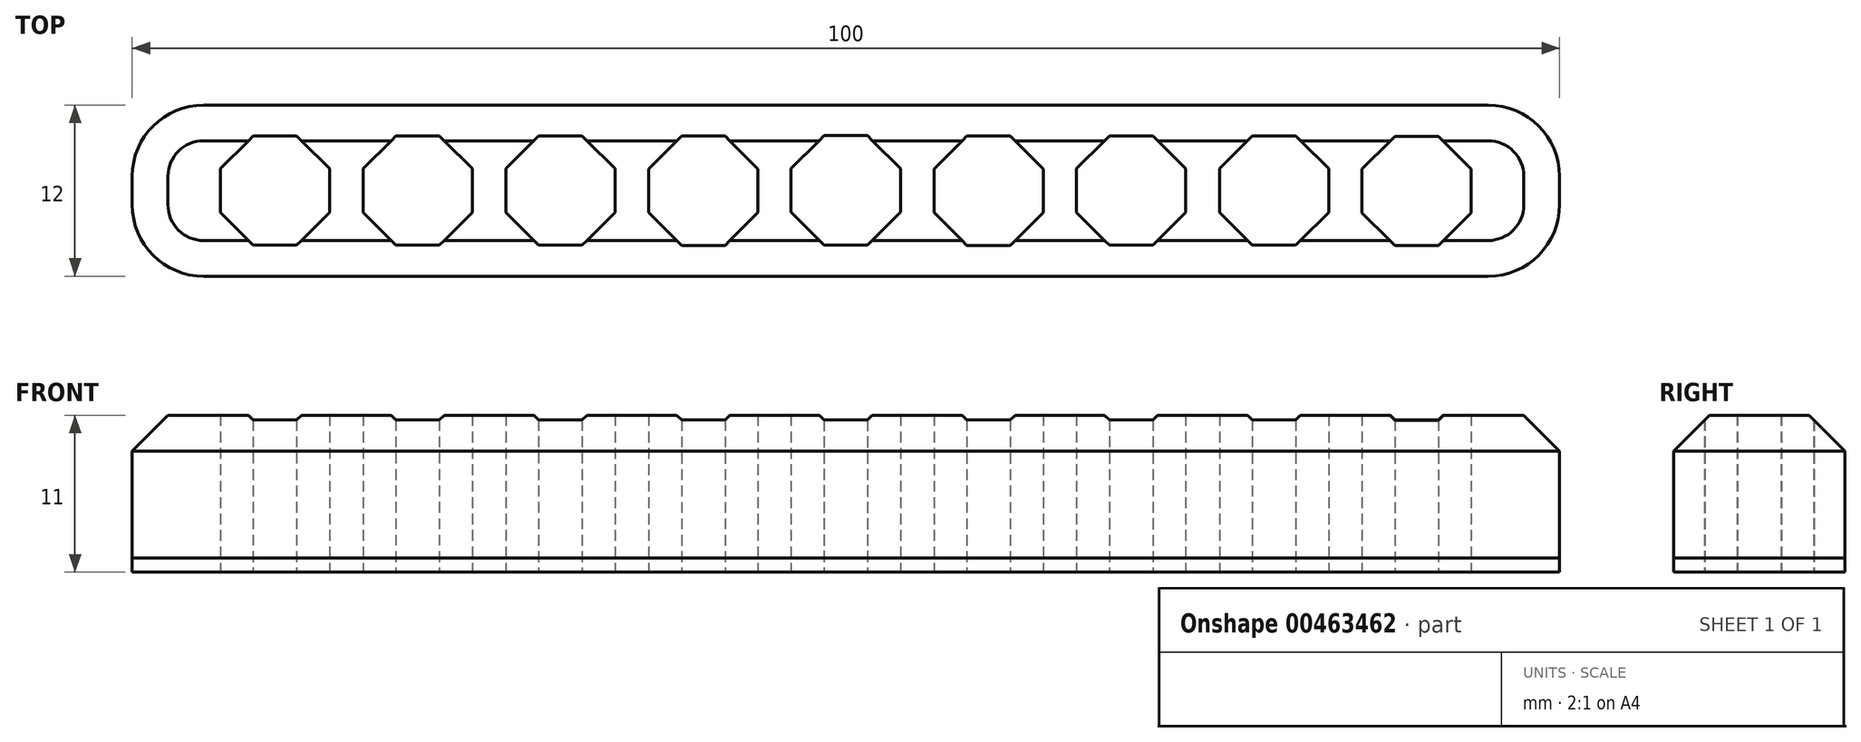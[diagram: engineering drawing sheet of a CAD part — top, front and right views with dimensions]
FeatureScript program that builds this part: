
annotation { "Feature Type Name" : "Feature", "Feature Type Description" : "" }
export const myFeature = defineFeature(function(context is Context, id is Id, definition is map)
    precondition{}
    {
        {
            var Q0;
            Q0=qCreatedBy(makeId("Top.planeOp"),FACE);
            var sketch = newSketch(context, id + "F0", { "sketchPlane" : qUnion([Q0])});
            skLineSegment(sketch, "E0.bottom", {"start": v(50, -6) * mm, "end": v(-50, -6) * mm});
            skLineSegment(sketch, "E0.top", {"start": v(50, 6) * mm, "end": v(-50, 6) * mm});
            skLineSegment(sketch, "E0.left", {"start": v(50, -6) * mm, "end": v(50, 6) * mm});
            skLineSegment(sketch, "E0.right", {"start": v(-50, -6) * mm, "end": v(-50, 6) * mm});
            skPoint(sketch, "E0.middle", {"position": v(0, 0) * mm});
            skPoint(sketch, "E1.middle", {"position": v(-40, 0) * mm});
            skLineSegment(sketch, "E2.bottom", {"start": v(-41.53, 3.83) * mm, "end": v(-38.47, 3.83) * mm});
            skLineSegment(sketch, "E2.top", {"start": v(-41.53, -3.83) * mm, "end": v(-38.47, -3.83) * mm});
            skLineSegment(sketch, "E2.left", {"start": v(-41.53, 3.83) * mm, "end": v(-41.53, -3.83) * mm});
            skLineSegment(sketch, "E2.right", {"start": v(-38.47, 3.83) * mm, "end": v(-38.47, -3.83) * mm});
            skLineSegment(sketch, "E3.bottom", {"start": v(-36.17, -1.54) * mm, "end": v(-43.83, -1.54) * mm});
            skLineSegment(sketch, "E3.top", {"start": v(-36.17, 1.54) * mm, "end": v(-43.83, 1.54) * mm});
            skLineSegment(sketch, "E3.left", {"start": v(-36.17, -1.54) * mm, "end": v(-36.17, 1.54) * mm});
            skLineSegment(sketch, "E3.right", {"start": v(-43.83, -1.54) * mm, "end": v(-43.83, 1.54) * mm});
            skPoint(sketch, "E4.middle", {"position": v(-30, 0) * mm});
            skLineSegment(sketch, "E5.bottom", {"start": v(-31.53, 3.83) * mm, "end": v(-28.47, 3.83) * mm});
            skLineSegment(sketch, "E5.top", {"start": v(-31.53, -3.83) * mm, "end": v(-28.47, -3.83) * mm});
            skLineSegment(sketch, "E5.left", {"start": v(-31.53, 3.83) * mm, "end": v(-31.53, -3.83) * mm});
            skLineSegment(sketch, "E5.right", {"start": v(-28.47, 3.83) * mm, "end": v(-28.47, -3.83) * mm});
            skLineSegment(sketch, "E6.bottom", {"start": v(-26.17, -1.54) * mm, "end": v(-33.83, -1.54) * mm});
            skLineSegment(sketch, "E6.top", {"start": v(-26.17, 1.54) * mm, "end": v(-33.83, 1.54) * mm});
            skLineSegment(sketch, "E6.left", {"start": v(-26.17, -1.54) * mm, "end": v(-26.17, 1.54) * mm});
            skLineSegment(sketch, "E6.right", {"start": v(-33.83, -1.54) * mm, "end": v(-33.83, 1.54) * mm});
            skPoint(sketch, "E7.middle", {"position": v(-20, 0) * mm});
            skLineSegment(sketch, "E8.bottom", {"start": v(-21.53, 3.84) * mm, "end": v(-18.48, 3.84) * mm});
            skLineSegment(sketch, "E8.top", {"start": v(-21.53, -3.83) * mm, "end": v(-18.48, -3.83) * mm});
            skLineSegment(sketch, "E8.left", {"start": v(-21.53, 3.84) * mm, "end": v(-21.53, -3.83) * mm});
            skLineSegment(sketch, "E8.right", {"start": v(-18.48, 3.84) * mm, "end": v(-18.48, -3.83) * mm});
            skLineSegment(sketch, "E9.bottom", {"start": v(-16.18, -1.53) * mm, "end": v(-23.83, -1.53) * mm});
            skLineSegment(sketch, "E9.top", {"start": v(-16.18, 1.54) * mm, "end": v(-23.83, 1.54) * mm});
            skLineSegment(sketch, "E9.left", {"start": v(-16.18, -1.53) * mm, "end": v(-16.18, 1.54) * mm});
            skLineSegment(sketch, "E9.right", {"start": v(-23.83, -1.53) * mm, "end": v(-23.83, 1.54) * mm});
            skPoint(sketch, "E10.middle", {"position": v(-9.99, 0) * mm});
            skLineSegment(sketch, "E11.bottom", {"start": v(-11.52, 3.83) * mm, "end": v(-8.46, 3.83) * mm});
            skLineSegment(sketch, "E11.top", {"start": v(-11.52, -3.84) * mm, "end": v(-8.46, -3.84) * mm});
            skLineSegment(sketch, "E11.left", {"start": v(-11.52, 3.83) * mm, "end": v(-11.52, -3.84) * mm});
            skLineSegment(sketch, "E11.right", {"start": v(-8.46, 3.83) * mm, "end": v(-8.46, -3.84) * mm});
            skLineSegment(sketch, "E12.bottom", {"start": v(-6.16, -1.54) * mm, "end": v(-13.82, -1.54) * mm});
            skLineSegment(sketch, "E12.top", {"start": v(-6.16, 1.53) * mm, "end": v(-13.82, 1.53) * mm});
            skLineSegment(sketch, "E12.left", {"start": v(-6.16, -1.54) * mm, "end": v(-6.16, 1.53) * mm});
            skLineSegment(sketch, "E12.right", {"start": v(-13.82, -1.54) * mm, "end": v(-13.82, 1.53) * mm});
            skPoint(sketch, "E13.middle", {"position": v(0, 0.02) * mm});
            skLineSegment(sketch, "E14.bottom", {"start": v(-1.53, 3.86) * mm, "end": v(1.52, 3.86) * mm});
            skLineSegment(sketch, "E14.top", {"start": v(-1.53, -3.8) * mm, "end": v(1.52, -3.8) * mm});
            skLineSegment(sketch, "E14.left", {"start": v(-1.53, 3.86) * mm, "end": v(-1.53, -3.8) * mm});
            skLineSegment(sketch, "E14.right", {"start": v(1.52, 3.86) * mm, "end": v(1.52, -3.8) * mm});
            skLineSegment(sketch, "E15.bottom", {"start": v(3.82, -1.51) * mm, "end": v(-3.83, -1.51) * mm});
            skLineSegment(sketch, "E15.top", {"start": v(3.82, 1.56) * mm, "end": v(-3.83, 1.56) * mm});
            skLineSegment(sketch, "E15.left", {"start": v(3.82, -1.51) * mm, "end": v(3.82, 1.56) * mm});
            skLineSegment(sketch, "E15.right", {"start": v(-3.83, -1.51) * mm, "end": v(-3.83, 1.56) * mm});
            skPoint(sketch, "E16.middle", {"position": v(10, 0) * mm});
            skLineSegment(sketch, "E17.bottom", {"start": v(8.48, 3.83) * mm, "end": v(11.53, 3.83) * mm});
            skLineSegment(sketch, "E17.top", {"start": v(8.48, -3.84) * mm, "end": v(11.53, -3.84) * mm});
            skLineSegment(sketch, "E17.left", {"start": v(8.48, 3.83) * mm, "end": v(8.48, -3.84) * mm});
            skLineSegment(sketch, "E17.right", {"start": v(11.53, 3.83) * mm, "end": v(11.53, -3.84) * mm});
            skLineSegment(sketch, "E18.bottom", {"start": v(13.83, -1.54) * mm, "end": v(6.18, -1.54) * mm});
            skLineSegment(sketch, "E18.top", {"start": v(13.83, 1.53) * mm, "end": v(6.18, 1.53) * mm});
            skLineSegment(sketch, "E18.left", {"start": v(13.83, -1.54) * mm, "end": v(13.83, 1.53) * mm});
            skLineSegment(sketch, "E18.right", {"start": v(6.18, -1.54) * mm, "end": v(6.18, 1.53) * mm});
            skPoint(sketch, "E19.middle", {"position": v(19.99, 0) * mm});
            skLineSegment(sketch, "E20.bottom", {"start": v(18.46, 3.84) * mm, "end": v(21.51, 3.84) * mm});
            skLineSegment(sketch, "E20.top", {"start": v(18.46, -3.82) * mm, "end": v(21.51, -3.82) * mm});
            skLineSegment(sketch, "E20.left", {"start": v(18.46, 3.84) * mm, "end": v(18.46, -3.82) * mm});
            skLineSegment(sketch, "E20.right", {"start": v(21.51, 3.84) * mm, "end": v(21.51, -3.82) * mm});
            skLineSegment(sketch, "E21.bottom", {"start": v(23.82, -1.53) * mm, "end": v(16.16, -1.53) * mm});
            skLineSegment(sketch, "E21.top", {"start": v(23.82, 1.55) * mm, "end": v(16.16, 1.55) * mm});
            skLineSegment(sketch, "E21.left", {"start": v(23.82, -1.53) * mm, "end": v(23.82, 1.55) * mm});
            skLineSegment(sketch, "E21.right", {"start": v(16.16, -1.53) * mm, "end": v(16.16, 1.55) * mm});
            skPoint(sketch, "E22.middle", {"position": v(30, 0) * mm});
            skLineSegment(sketch, "E23.bottom", {"start": v(28.47, 3.84) * mm, "end": v(31.53, 3.84) * mm});
            skLineSegment(sketch, "E23.top", {"start": v(28.47, -3.82) * mm, "end": v(31.53, -3.82) * mm});
            skLineSegment(sketch, "E23.left", {"start": v(28.47, 3.84) * mm, "end": v(28.47, -3.82) * mm});
            skLineSegment(sketch, "E23.right", {"start": v(31.53, 3.84) * mm, "end": v(31.53, -3.82) * mm});
            skLineSegment(sketch, "E24.bottom", {"start": v(33.83, -1.53) * mm, "end": v(26.17, -1.53) * mm});
            skLineSegment(sketch, "E24.top", {"start": v(33.83, 1.55) * mm, "end": v(26.17, 1.55) * mm});
            skLineSegment(sketch, "E24.left", {"start": v(33.83, -1.53) * mm, "end": v(33.83, 1.55) * mm});
            skLineSegment(sketch, "E24.right", {"start": v(26.17, -1.53) * mm, "end": v(26.17, 1.55) * mm});
            skPoint(sketch, "E25.middle", {"position": v(40, -0.02) * mm});
            skLineSegment(sketch, "E26.bottom", {"start": v(38.47, 3.81) * mm, "end": v(41.52, 3.81) * mm});
            skLineSegment(sketch, "E26.top", {"start": v(38.47, -3.85) * mm, "end": v(41.52, -3.85) * mm});
            skLineSegment(sketch, "E26.left", {"start": v(38.47, 3.81) * mm, "end": v(38.47, -3.85) * mm});
            skLineSegment(sketch, "E26.right", {"start": v(41.52, 3.81) * mm, "end": v(41.52, -3.85) * mm});
            skLineSegment(sketch, "E27.bottom", {"start": v(43.82, -1.56) * mm, "end": v(36.17, -1.56) * mm});
            skLineSegment(sketch, "E27.top", {"start": v(43.82, 1.52) * mm, "end": v(36.17, 1.52) * mm});
            skLineSegment(sketch, "E27.left", {"start": v(43.82, -1.56) * mm, "end": v(43.82, 1.52) * mm});
            skLineSegment(sketch, "E27.right", {"start": v(36.17, -1.56) * mm, "end": v(36.17, 1.52) * mm});
            skLineSegment(sketch, "E28", {"start": v(-41.53, 3.83) * mm, "end": v(-43.83, 1.54) * mm});
            skLineSegment(sketch, "E29", {"start": v(-43.83, -1.54) * mm, "end": v(-41.53, -3.83) * mm});
            skLineSegment(sketch, "E30", {"start": v(-38.47, -3.83) * mm, "end": v(-36.17, -1.54) * mm});
            skLineSegment(sketch, "E31", {"start": v(-36.17, 1.54) * mm, "end": v(-38.47, 3.83) * mm});
            skLineSegment(sketch, "E32", {"start": v(-33.83, 1.54) * mm, "end": v(-31.53, 3.83) * mm});
            skLineSegment(sketch, "E33", {"start": v(-28.47, 3.83) * mm, "end": v(-26.17, 1.54) * mm});
            skLineSegment(sketch, "E34", {"start": v(-26.17, -1.54) * mm, "end": v(-28.47, -3.83) * mm});
            skLineSegment(sketch, "E35", {"start": v(-31.53, -3.83) * mm, "end": v(-33.83, -1.54) * mm});
            skLineSegment(sketch, "E36", {"start": v(-23.83, 1.54) * mm, "end": v(-21.53, 3.84) * mm});
            skLineSegment(sketch, "E37", {"start": v(-18.48, 3.84) * mm, "end": v(-16.18, 1.54) * mm});
            skLineSegment(sketch, "E38", {"start": v(-16.18, -1.53) * mm, "end": v(-18.48, -3.83) * mm});
            skLineSegment(sketch, "E39", {"start": v(-21.53, -3.83) * mm, "end": v(-23.83, -1.53) * mm});
            skLineSegment(sketch, "E40", {"start": v(-13.82, -1.54) * mm, "end": v(-11.52, -3.84) * mm});
            skLineSegment(sketch, "E41", {"start": v(-13.82, 1.53) * mm, "end": v(-11.52, 3.83) * mm});
            skLineSegment(sketch, "E42", {"start": v(-8.46, 3.83) * mm, "end": v(-6.16, 1.53) * mm});
            skLineSegment(sketch, "E43", {"start": v(-6.16, -1.54) * mm, "end": v(-8.46, -3.84) * mm});
            skLineSegment(sketch, "E44", {"start": v(-3.83, -1.51) * mm, "end": v(-1.53, -3.8) * mm});
            skLineSegment(sketch, "E45", {"start": v(-3.83, 1.56) * mm, "end": v(-1.53, 3.86) * mm});
            skLineSegment(sketch, "E46", {"start": v(1.52, 3.86) * mm, "end": v(3.82, 1.56) * mm});
            skLineSegment(sketch, "E47", {"start": v(3.82, -1.51) * mm, "end": v(1.52, -3.8) * mm});
            skLineSegment(sketch, "E48", {"start": v(6.18, 1.53) * mm, "end": v(8.48, 3.83) * mm});
            skLineSegment(sketch, "E49", {"start": v(11.53, 3.83) * mm, "end": v(13.83, 1.53) * mm});
            skLineSegment(sketch, "E50", {"start": v(13.83, -1.54) * mm, "end": v(11.53, -3.84) * mm});
            skLineSegment(sketch, "E51", {"start": v(8.48, -3.84) * mm, "end": v(6.18, -1.54) * mm});
            skLineSegment(sketch, "E52", {"start": v(16.16, 1.55) * mm, "end": v(18.46, 3.84) * mm});
            skLineSegment(sketch, "E53", {"start": v(21.51, 3.84) * mm, "end": v(23.82, 1.55) * mm});
            skLineSegment(sketch, "E54", {"start": v(23.82, -1.53) * mm, "end": v(21.51, -3.82) * mm});
            skLineSegment(sketch, "E55", {"start": v(18.46, -3.82) * mm, "end": v(16.16, -1.53) * mm});
            skLineSegment(sketch, "E56", {"start": v(26.17, 1.55) * mm, "end": v(28.47, 3.84) * mm});
            skLineSegment(sketch, "E57", {"start": v(31.53, 3.84) * mm, "end": v(33.83, 1.55) * mm});
            skLineSegment(sketch, "E58", {"start": v(33.83, -1.53) * mm, "end": v(31.53, -3.82) * mm});
            skLineSegment(sketch, "E59", {"start": v(28.47, -3.82) * mm, "end": v(26.17, -1.53) * mm});
            skLineSegment(sketch, "E60", {"start": v(36.17, 1.52) * mm, "end": v(38.47, 3.81) * mm});
            skLineSegment(sketch, "E61", {"start": v(41.52, 3.81) * mm, "end": v(43.82, 1.52) * mm});
            skLineSegment(sketch, "E62", {"start": v(43.82, -1.56) * mm, "end": v(41.52, -3.85) * mm});
            skLineSegment(sketch, "E63", {"start": v(38.47, -3.85) * mm, "end": v(36.17, -1.56) * mm});
            skSolve(sketch);
        }
        {
            var Q0;
            Q0=makeQuery(id+"F0.imprint","IMPRINT",FACE,{"disambiguationData":[TD([[makeQuery(id+"F0.imprint","IMPRINT",EDGE,{"derivedFrom":sQuery(id+"F0.wireOp",EDGE,"E0.bottom")}),-1.0]])]});
            extrude(context, id + "F1", {"entities" : qUnion([Q0]), "depth" : 11 * mm});
        }
        {
            var Q0;
            Q0=makeQuery(id+"F0.imprint","IMPRINT",FACE,{"disambiguationData":[TD([[makeQuery(id+"F0.imprint","IMPRINT",EDGE,{"derivedFrom":sQuery(id+"F0.wireOp",EDGE,"E0.bottom")}),-1.0]])]});
            var Q1;
            {var subQ5=sQuery(id+"F0.wireOp",EDGE,"E3.right");Q1=makeQuery(id+"F0.imprint","IMPRINT",FACE,{"disambiguationData":[TD([[makeQuery(id+"F0.imprint","IMPRINT",EDGE,{"derivedFrom":subQ5}),-1.0]])]});}
            var Q2;
            {var subQ0=sQuery(id+"F0.wireOp",EDGE,"E28");Q2=makeQuery(id+"F0.imprint","IMPRINT",FACE,{"disambiguationData":[TD([[makeQuery(id+"F0.imprint","IMPRINT",EDGE,{"derivedFrom":subQ0}),1.0]])]});}
            var Q3;
            {var subQ0=sQuery(id+"F0.wireOp",EDGE,"E2.bottom");Q3=makeQuery(id+"F0.imprint","IMPRINT",FACE,{"disambiguationData":[TD([[makeQuery(id+"F0.imprint","IMPRINT",EDGE,{"derivedFrom":subQ0}),-1.0]])]});}
            var Q4;
            {var subQ0=sQuery(id+"F0.wireOp",EDGE,"E29");Q4=makeQuery(id+"F0.imprint","IMPRINT",FACE,{"disambiguationData":[TD([[makeQuery(id+"F0.imprint","IMPRINT",EDGE,{"derivedFrom":subQ0}),1.0]])]});}
            var Q5;
            {var subQ0=sQuery(id+"F0.wireOp",EDGE,"E2.top");Q5=makeQuery(id+"F0.imprint","IMPRINT",FACE,{"disambiguationData":[TD([[makeQuery(id+"F0.imprint","IMPRINT",EDGE,{"derivedFrom":subQ0}),1.0]])]});}
            var Q6;
            {var subQ0=sQuery(id+"F0.wireOp",EDGE,"E3.top");var subQ1=sQuery(id+"F0.wireOp",EDGE,"E2.left");var subQ2=makeQuery(id+"F0.imprint","INTERSECT",VERTEX,{"derivedFrom":[subQ1,subQ0]});Q6=makeQuery(id+"F0.imprint","IMPRINT",FACE,{"disambiguationData":[TD([[makeQuery(id+"F0.imprint","IMPRINT",EDGE,{"disambiguationData":[TD([[subQ2,-1.0]])],"derivedFrom":subQ1}),1.0]])]});}
            var Q7;
            {var subQ5=sQuery(id+"F0.wireOp",EDGE,"E3.left");Q7=makeQuery(id+"F0.imprint","IMPRINT",FACE,{"disambiguationData":[TD([[makeQuery(id+"F0.imprint","IMPRINT",EDGE,{"derivedFrom":subQ5}),1.0]])]});}
            var Q8;
            {var subQ0=sQuery(id+"F0.wireOp",EDGE,"E31");Q8=makeQuery(id+"F0.imprint","IMPRINT",FACE,{"disambiguationData":[TD([[makeQuery(id+"F0.imprint","IMPRINT",EDGE,{"derivedFrom":subQ0}),1.0]])]});}
            var Q9;
            {var subQ0=sQuery(id+"F0.wireOp",EDGE,"E30");Q9=makeQuery(id+"F0.imprint","IMPRINT",FACE,{"disambiguationData":[TD([[makeQuery(id+"F0.imprint","IMPRINT",EDGE,{"derivedFrom":subQ0}),1.0]])]});}
            var Q10;
            {var subQ0=sQuery(id+"F0.wireOp",EDGE,"E35");Q10=makeQuery(id+"F0.imprint","IMPRINT",FACE,{"disambiguationData":[TD([[makeQuery(id+"F0.imprint","IMPRINT",EDGE,{"derivedFrom":subQ0}),-1.0]])]});}
            var Q11;
            {var subQ5=sQuery(id+"F0.wireOp",EDGE,"E6.right");Q11=makeQuery(id+"F0.imprint","IMPRINT",FACE,{"disambiguationData":[TD([[makeQuery(id+"F0.imprint","IMPRINT",EDGE,{"derivedFrom":subQ5}),-1.0]])]});}
            var Q12;
            {var subQ0=sQuery(id+"F0.wireOp",EDGE,"E32");Q12=makeQuery(id+"F0.imprint","IMPRINT",FACE,{"disambiguationData":[TD([[makeQuery(id+"F0.imprint","IMPRINT",EDGE,{"derivedFrom":subQ0}),-1.0]])]});}
            var Q13;
            {var subQ0=sQuery(id+"F0.wireOp",EDGE,"E5.bottom");Q13=makeQuery(id+"F0.imprint","IMPRINT",FACE,{"disambiguationData":[TD([[makeQuery(id+"F0.imprint","IMPRINT",EDGE,{"derivedFrom":subQ0}),-1.0]])]});}
            var Q14;
            {var subQ0=sQuery(id+"F0.wireOp",EDGE,"E33");Q14=makeQuery(id+"F0.imprint","IMPRINT",FACE,{"disambiguationData":[TD([[makeQuery(id+"F0.imprint","IMPRINT",EDGE,{"derivedFrom":subQ0}),-1.0]])]});}
            var Q15;
            {var subQ5=sQuery(id+"F0.wireOp",EDGE,"E6.left");Q15=makeQuery(id+"F0.imprint","IMPRINT",FACE,{"disambiguationData":[TD([[makeQuery(id+"F0.imprint","IMPRINT",EDGE,{"derivedFrom":subQ5}),1.0]])]});}
            var Q16;
            {var subQ0=sQuery(id+"F0.wireOp",EDGE,"E6.top");var subQ1=sQuery(id+"F0.wireOp",EDGE,"E5.left");var subQ2=makeQuery(id+"F0.imprint","INTERSECT",VERTEX,{"derivedFrom":[subQ1,subQ0]});Q16=makeQuery(id+"F0.imprint","IMPRINT",FACE,{"disambiguationData":[TD([[makeQuery(id+"F0.imprint","IMPRINT",EDGE,{"disambiguationData":[TD([[subQ2,-1.0]])],"derivedFrom":subQ1}),1.0]])]});}
            var Q17;
            {var subQ0=sQuery(id+"F0.wireOp",EDGE,"E5.top");Q17=makeQuery(id+"F0.imprint","IMPRINT",FACE,{"disambiguationData":[TD([[makeQuery(id+"F0.imprint","IMPRINT",EDGE,{"derivedFrom":subQ0}),1.0]])]});}
            var Q18;
            {var subQ0=sQuery(id+"F0.wireOp",EDGE,"E34");Q18=makeQuery(id+"F0.imprint","IMPRINT",FACE,{"disambiguationData":[TD([[makeQuery(id+"F0.imprint","IMPRINT",EDGE,{"derivedFrom":subQ0}),-1.0]])]});}
            var Q19;
            {var subQ0=sQuery(id+"F0.wireOp",EDGE,"E39");Q19=makeQuery(id+"F0.imprint","IMPRINT",FACE,{"disambiguationData":[TD([[makeQuery(id+"F0.imprint","IMPRINT",EDGE,{"derivedFrom":subQ0}),-1.0]])]});}
            var Q20;
            {var subQ5=sQuery(id+"F0.wireOp",EDGE,"E9.right");Q20=makeQuery(id+"F0.imprint","IMPRINT",FACE,{"disambiguationData":[TD([[makeQuery(id+"F0.imprint","IMPRINT",EDGE,{"derivedFrom":subQ5}),-1.0]])]});}
            var Q21;
            {var subQ0=sQuery(id+"F0.wireOp",EDGE,"E36");Q21=makeQuery(id+"F0.imprint","IMPRINT",FACE,{"disambiguationData":[TD([[makeQuery(id+"F0.imprint","IMPRINT",EDGE,{"derivedFrom":subQ0}),-1.0]])]});}
            var Q22;
            {var subQ0=sQuery(id+"F0.wireOp",EDGE,"E8.bottom");Q22=makeQuery(id+"F0.imprint","IMPRINT",FACE,{"disambiguationData":[TD([[makeQuery(id+"F0.imprint","IMPRINT",EDGE,{"derivedFrom":subQ0}),-1.0]])]});}
            var Q23;
            {var subQ0=sQuery(id+"F0.wireOp",EDGE,"E9.top");var subQ1=sQuery(id+"F0.wireOp",EDGE,"E8.left");var subQ2=makeQuery(id+"F0.imprint","INTERSECT",VERTEX,{"derivedFrom":[subQ1,subQ0]});Q23=makeQuery(id+"F0.imprint","IMPRINT",FACE,{"disambiguationData":[TD([[makeQuery(id+"F0.imprint","IMPRINT",EDGE,{"disambiguationData":[TD([[subQ2,-1.0]])],"derivedFrom":subQ1}),1.0]])]});}
            var Q24;
            {var subQ0=sQuery(id+"F0.wireOp",EDGE,"E8.top");Q24=makeQuery(id+"F0.imprint","IMPRINT",FACE,{"disambiguationData":[TD([[makeQuery(id+"F0.imprint","IMPRINT",EDGE,{"derivedFrom":subQ0}),1.0]])]});}
            var Q25;
            {var subQ0=sQuery(id+"F0.wireOp",EDGE,"E38");Q25=makeQuery(id+"F0.imprint","IMPRINT",FACE,{"disambiguationData":[TD([[makeQuery(id+"F0.imprint","IMPRINT",EDGE,{"derivedFrom":subQ0}),-1.0]])]});}
            var Q26;
            {var subQ5=sQuery(id+"F0.wireOp",EDGE,"E9.left");Q26=makeQuery(id+"F0.imprint","IMPRINT",FACE,{"disambiguationData":[TD([[makeQuery(id+"F0.imprint","IMPRINT",EDGE,{"derivedFrom":subQ5}),1.0]])]});}
            var Q27;
            {var subQ0=sQuery(id+"F0.wireOp",EDGE,"E37");Q27=makeQuery(id+"F0.imprint","IMPRINT",FACE,{"disambiguationData":[TD([[makeQuery(id+"F0.imprint","IMPRINT",EDGE,{"derivedFrom":subQ0}),-1.0]])]});}
            var Q28;
            {var subQ0=sQuery(id+"F0.wireOp",EDGE,"E41");Q28=makeQuery(id+"F0.imprint","IMPRINT",FACE,{"disambiguationData":[TD([[makeQuery(id+"F0.imprint","IMPRINT",EDGE,{"derivedFrom":subQ0}),-1.0]])]});}
            var Q29;
            {var subQ5=sQuery(id+"F0.wireOp",EDGE,"E12.right");Q29=makeQuery(id+"F0.imprint","IMPRINT",FACE,{"disambiguationData":[TD([[makeQuery(id+"F0.imprint","IMPRINT",EDGE,{"derivedFrom":subQ5}),-1.0]])]});}
            var Q30;
            {var subQ0=sQuery(id+"F0.wireOp",EDGE,"E40");Q30=makeQuery(id+"F0.imprint","IMPRINT",FACE,{"disambiguationData":[TD([[makeQuery(id+"F0.imprint","IMPRINT",EDGE,{"derivedFrom":subQ0}),1.0]])]});}
            var Q31;
            {var subQ0=sQuery(id+"F0.wireOp",EDGE,"E11.top");Q31=makeQuery(id+"F0.imprint","IMPRINT",FACE,{"disambiguationData":[TD([[makeQuery(id+"F0.imprint","IMPRINT",EDGE,{"derivedFrom":subQ0}),1.0]])]});}
            var Q32;
            {var subQ0=sQuery(id+"F0.wireOp",EDGE,"E11.bottom");Q32=makeQuery(id+"F0.imprint","IMPRINT",FACE,{"disambiguationData":[TD([[makeQuery(id+"F0.imprint","IMPRINT",EDGE,{"derivedFrom":subQ0}),-1.0]])]});}
            var Q33;
            {var subQ5=sQuery(id+"F0.wireOp",EDGE,"E12.left");Q33=makeQuery(id+"F0.imprint","IMPRINT",FACE,{"disambiguationData":[TD([[makeQuery(id+"F0.imprint","IMPRINT",EDGE,{"derivedFrom":subQ5}),1.0]])]});}
            var Q34;
            {var subQ0=sQuery(id+"F0.wireOp",EDGE,"E42");Q34=makeQuery(id+"F0.imprint","IMPRINT",FACE,{"disambiguationData":[TD([[makeQuery(id+"F0.imprint","IMPRINT",EDGE,{"derivedFrom":subQ0}),-1.0]])]});}
            var Q35;
            {var subQ0=sQuery(id+"F0.wireOp",EDGE,"E43");Q35=makeQuery(id+"F0.imprint","IMPRINT",FACE,{"disambiguationData":[TD([[makeQuery(id+"F0.imprint","IMPRINT",EDGE,{"derivedFrom":subQ0}),-1.0]])]});}
            var Q36;
            {var subQ0=sQuery(id+"F0.wireOp",EDGE,"E12.top");var subQ1=sQuery(id+"F0.wireOp",EDGE,"E11.left");var subQ2=makeQuery(id+"F0.imprint","INTERSECT",VERTEX,{"derivedFrom":[subQ1,subQ0]});Q36=makeQuery(id+"F0.imprint","IMPRINT",FACE,{"disambiguationData":[TD([[makeQuery(id+"F0.imprint","IMPRINT",EDGE,{"disambiguationData":[TD([[subQ2,-1.0]])],"derivedFrom":subQ1}),1.0]])]});}
            var Q37;
            {var subQ0=sQuery(id+"F0.wireOp",EDGE,"E45");Q37=makeQuery(id+"F0.imprint","IMPRINT",FACE,{"disambiguationData":[TD([[makeQuery(id+"F0.imprint","IMPRINT",EDGE,{"derivedFrom":subQ0}),-1.0]])]});}
            var Q38;
            {var subQ0=sQuery(id+"F0.wireOp",EDGE,"E14.bottom");Q38=makeQuery(id+"F0.imprint","IMPRINT",FACE,{"disambiguationData":[TD([[makeQuery(id+"F0.imprint","IMPRINT",EDGE,{"derivedFrom":subQ0}),-1.0]])]});}
            var Q39;
            {var subQ0=sQuery(id+"F0.wireOp",EDGE,"E46");Q39=makeQuery(id+"F0.imprint","IMPRINT",FACE,{"disambiguationData":[TD([[makeQuery(id+"F0.imprint","IMPRINT",EDGE,{"derivedFrom":subQ0}),-1.0]])]});}
            var Q40;
            {var subQ5=sQuery(id+"F0.wireOp",EDGE,"E15.left");Q40=makeQuery(id+"F0.imprint","IMPRINT",FACE,{"disambiguationData":[TD([[makeQuery(id+"F0.imprint","IMPRINT",EDGE,{"derivedFrom":subQ5}),1.0]])]});}
            var Q41;
            {var subQ0=sQuery(id+"F0.wireOp",EDGE,"E15.top");var subQ1=sQuery(id+"F0.wireOp",EDGE,"E14.left");var subQ2=makeQuery(id+"F0.imprint","INTERSECT",VERTEX,{"derivedFrom":[subQ1,subQ0]});Q41=makeQuery(id+"F0.imprint","IMPRINT",FACE,{"disambiguationData":[TD([[makeQuery(id+"F0.imprint","IMPRINT",EDGE,{"disambiguationData":[TD([[subQ2,-1.0]])],"derivedFrom":subQ1}),1.0]])]});}
            var Q42;
            {var subQ5=sQuery(id+"F0.wireOp",EDGE,"E15.right");Q42=makeQuery(id+"F0.imprint","IMPRINT",FACE,{"disambiguationData":[TD([[makeQuery(id+"F0.imprint","IMPRINT",EDGE,{"derivedFrom":subQ5}),-1.0]])]});}
            var Q43;
            {var subQ0=sQuery(id+"F0.wireOp",EDGE,"E14.top");Q43=makeQuery(id+"F0.imprint","IMPRINT",FACE,{"disambiguationData":[TD([[makeQuery(id+"F0.imprint","IMPRINT",EDGE,{"derivedFrom":subQ0}),1.0]])]});}
            var Q44;
            {var subQ0=sQuery(id+"F0.wireOp",EDGE,"E47");Q44=makeQuery(id+"F0.imprint","IMPRINT",FACE,{"disambiguationData":[TD([[makeQuery(id+"F0.imprint","IMPRINT",EDGE,{"derivedFrom":subQ0}),-1.0]])]});}
            var Q45;
            {var subQ0=sQuery(id+"F0.wireOp",EDGE,"E44");Q45=makeQuery(id+"F0.imprint","IMPRINT",FACE,{"disambiguationData":[TD([[makeQuery(id+"F0.imprint","IMPRINT",EDGE,{"derivedFrom":subQ0}),1.0]])]});}
            var Q46;
            {var subQ5=sQuery(id+"F0.wireOp",EDGE,"E18.right");Q46=makeQuery(id+"F0.imprint","IMPRINT",FACE,{"disambiguationData":[TD([[makeQuery(id+"F0.imprint","IMPRINT",EDGE,{"derivedFrom":subQ5}),-1.0]])]});}
            var Q47;
            {var subQ0=sQuery(id+"F0.wireOp",EDGE,"E48");Q47=makeQuery(id+"F0.imprint","IMPRINT",FACE,{"disambiguationData":[TD([[makeQuery(id+"F0.imprint","IMPRINT",EDGE,{"derivedFrom":subQ0}),-1.0]])]});}
            var Q48;
            {var subQ0=sQuery(id+"F0.wireOp",EDGE,"E17.bottom");Q48=makeQuery(id+"F0.imprint","IMPRINT",FACE,{"disambiguationData":[TD([[makeQuery(id+"F0.imprint","IMPRINT",EDGE,{"derivedFrom":subQ0}),-1.0]])]});}
            var Q49;
            {var subQ0=sQuery(id+"F0.wireOp",EDGE,"E49");Q49=makeQuery(id+"F0.imprint","IMPRINT",FACE,{"disambiguationData":[TD([[makeQuery(id+"F0.imprint","IMPRINT",EDGE,{"derivedFrom":subQ0}),-1.0]])]});}
            var Q50;
            {var subQ5=sQuery(id+"F0.wireOp",EDGE,"E18.left");Q50=makeQuery(id+"F0.imprint","IMPRINT",FACE,{"disambiguationData":[TD([[makeQuery(id+"F0.imprint","IMPRINT",EDGE,{"derivedFrom":subQ5}),1.0]])]});}
            var Q51;
            {var subQ0=sQuery(id+"F0.wireOp",EDGE,"E18.top");var subQ1=sQuery(id+"F0.wireOp",EDGE,"E17.left");var subQ2=makeQuery(id+"F0.imprint","INTERSECT",VERTEX,{"derivedFrom":[subQ1,subQ0]});Q51=makeQuery(id+"F0.imprint","IMPRINT",FACE,{"disambiguationData":[TD([[makeQuery(id+"F0.imprint","IMPRINT",EDGE,{"disambiguationData":[TD([[subQ2,-1.0]])],"derivedFrom":subQ1}),1.0]])]});}
            var Q52;
            {var subQ0=sQuery(id+"F0.wireOp",EDGE,"E51");Q52=makeQuery(id+"F0.imprint","IMPRINT",FACE,{"disambiguationData":[TD([[makeQuery(id+"F0.imprint","IMPRINT",EDGE,{"derivedFrom":subQ0}),-1.0]])]});}
            var Q53;
            {var subQ0=sQuery(id+"F0.wireOp",EDGE,"E17.top");Q53=makeQuery(id+"F0.imprint","IMPRINT",FACE,{"disambiguationData":[TD([[makeQuery(id+"F0.imprint","IMPRINT",EDGE,{"derivedFrom":subQ0}),1.0]])]});}
            var Q54;
            {var subQ0=sQuery(id+"F0.wireOp",EDGE,"E50");Q54=makeQuery(id+"F0.imprint","IMPRINT",FACE,{"disambiguationData":[TD([[makeQuery(id+"F0.imprint","IMPRINT",EDGE,{"derivedFrom":subQ0}),-1.0]])]});}
            var Q55;
            {var subQ5=sQuery(id+"F0.wireOp",EDGE,"E21.right");Q55=makeQuery(id+"F0.imprint","IMPRINT",FACE,{"disambiguationData":[TD([[makeQuery(id+"F0.imprint","IMPRINT",EDGE,{"derivedFrom":subQ5}),-1.0]])]});}
            var Q56;
            {var subQ0=sQuery(id+"F0.wireOp",EDGE,"E55");Q56=makeQuery(id+"F0.imprint","IMPRINT",FACE,{"disambiguationData":[TD([[makeQuery(id+"F0.imprint","IMPRINT",EDGE,{"derivedFrom":subQ0}),-1.0]])]});}
            var Q57;
            {var subQ0=sQuery(id+"F0.wireOp",EDGE,"E20.top");Q57=makeQuery(id+"F0.imprint","IMPRINT",FACE,{"disambiguationData":[TD([[makeQuery(id+"F0.imprint","IMPRINT",EDGE,{"derivedFrom":subQ0}),1.0]])]});}
            var Q58;
            {var subQ0=sQuery(id+"F0.wireOp",EDGE,"E54");Q58=makeQuery(id+"F0.imprint","IMPRINT",FACE,{"disambiguationData":[TD([[makeQuery(id+"F0.imprint","IMPRINT",EDGE,{"derivedFrom":subQ0}),-1.0]])]});}
            var Q59;
            {var subQ5=sQuery(id+"F0.wireOp",EDGE,"E21.left");Q59=makeQuery(id+"F0.imprint","IMPRINT",FACE,{"disambiguationData":[TD([[makeQuery(id+"F0.imprint","IMPRINT",EDGE,{"derivedFrom":subQ5}),1.0]])]});}
            var Q60;
            {var subQ0=sQuery(id+"F0.wireOp",EDGE,"E21.top");var subQ1=sQuery(id+"F0.wireOp",EDGE,"E20.left");var subQ2=makeQuery(id+"F0.imprint","INTERSECT",VERTEX,{"derivedFrom":[subQ1,subQ0]});Q60=makeQuery(id+"F0.imprint","IMPRINT",FACE,{"disambiguationData":[TD([[makeQuery(id+"F0.imprint","IMPRINT",EDGE,{"disambiguationData":[TD([[subQ2,-1.0]])],"derivedFrom":subQ1}),1.0]])]});}
            var Q61;
            {var subQ0=sQuery(id+"F0.wireOp",EDGE,"E20.bottom");Q61=makeQuery(id+"F0.imprint","IMPRINT",FACE,{"disambiguationData":[TD([[makeQuery(id+"F0.imprint","IMPRINT",EDGE,{"derivedFrom":subQ0}),-1.0]])]});}
            var Q62;
            {var subQ0=sQuery(id+"F0.wireOp",EDGE,"E52");Q62=makeQuery(id+"F0.imprint","IMPRINT",FACE,{"disambiguationData":[TD([[makeQuery(id+"F0.imprint","IMPRINT",EDGE,{"derivedFrom":subQ0}),-1.0]])]});}
            var Q63;
            {var subQ0=sQuery(id+"F0.wireOp",EDGE,"E53");Q63=makeQuery(id+"F0.imprint","IMPRINT",FACE,{"disambiguationData":[TD([[makeQuery(id+"F0.imprint","IMPRINT",EDGE,{"derivedFrom":subQ0}),-1.0]])]});}
            var Q64;
            {var subQ0=sQuery(id+"F0.wireOp",EDGE,"E56");Q64=makeQuery(id+"F0.imprint","IMPRINT",FACE,{"disambiguationData":[TD([[makeQuery(id+"F0.imprint","IMPRINT",EDGE,{"derivedFrom":subQ0}),-1.0]])]});}
            var Q65;
            {var subQ5=sQuery(id+"F0.wireOp",EDGE,"E24.right");Q65=makeQuery(id+"F0.imprint","IMPRINT",FACE,{"disambiguationData":[TD([[makeQuery(id+"F0.imprint","IMPRINT",EDGE,{"derivedFrom":subQ5}),-1.0]])]});}
            var Q66;
            {var subQ0=sQuery(id+"F0.wireOp",EDGE,"E59");Q66=makeQuery(id+"F0.imprint","IMPRINT",FACE,{"disambiguationData":[TD([[makeQuery(id+"F0.imprint","IMPRINT",EDGE,{"derivedFrom":subQ0}),-1.0]])]});}
            var Q67;
            {var subQ0=sQuery(id+"F0.wireOp",EDGE,"E23.top");Q67=makeQuery(id+"F0.imprint","IMPRINT",FACE,{"disambiguationData":[TD([[makeQuery(id+"F0.imprint","IMPRINT",EDGE,{"derivedFrom":subQ0}),1.0]])]});}
            var Q68;
            {var subQ0=sQuery(id+"F0.wireOp",EDGE,"E24.top");var subQ1=sQuery(id+"F0.wireOp",EDGE,"E23.left");var subQ2=makeQuery(id+"F0.imprint","INTERSECT",VERTEX,{"derivedFrom":[subQ1,subQ0]});Q68=makeQuery(id+"F0.imprint","IMPRINT",FACE,{"disambiguationData":[TD([[makeQuery(id+"F0.imprint","IMPRINT",EDGE,{"disambiguationData":[TD([[subQ2,-1.0]])],"derivedFrom":subQ1}),1.0]])]});}
            var Q69;
            {var subQ0=sQuery(id+"F0.wireOp",EDGE,"E23.bottom");Q69=makeQuery(id+"F0.imprint","IMPRINT",FACE,{"disambiguationData":[TD([[makeQuery(id+"F0.imprint","IMPRINT",EDGE,{"derivedFrom":subQ0}),-1.0]])]});}
            var Q70;
            {var subQ0=sQuery(id+"F0.wireOp",EDGE,"E57");Q70=makeQuery(id+"F0.imprint","IMPRINT",FACE,{"disambiguationData":[TD([[makeQuery(id+"F0.imprint","IMPRINT",EDGE,{"derivedFrom":subQ0}),-1.0]])]});}
            var Q71;
            {var subQ5=sQuery(id+"F0.wireOp",EDGE,"E24.left");Q71=makeQuery(id+"F0.imprint","IMPRINT",FACE,{"disambiguationData":[TD([[makeQuery(id+"F0.imprint","IMPRINT",EDGE,{"derivedFrom":subQ5}),1.0]])]});}
            var Q72;
            {var subQ0=sQuery(id+"F0.wireOp",EDGE,"E58");Q72=makeQuery(id+"F0.imprint","IMPRINT",FACE,{"disambiguationData":[TD([[makeQuery(id+"F0.imprint","IMPRINT",EDGE,{"derivedFrom":subQ0}),-1.0]])]});}
            var Q73;
            {var subQ5=sQuery(id+"F0.wireOp",EDGE,"E27.right");Q73=makeQuery(id+"F0.imprint","IMPRINT",FACE,{"disambiguationData":[TD([[makeQuery(id+"F0.imprint","IMPRINT",EDGE,{"derivedFrom":subQ5}),-1.0]])]});}
            var Q74;
            {var subQ0=sQuery(id+"F0.wireOp",EDGE,"E63");Q74=makeQuery(id+"F0.imprint","IMPRINT",FACE,{"disambiguationData":[TD([[makeQuery(id+"F0.imprint","IMPRINT",EDGE,{"derivedFrom":subQ0}),-1.0]])]});}
            var Q75;
            {var subQ0=sQuery(id+"F0.wireOp",EDGE,"E26.top");Q75=makeQuery(id+"F0.imprint","IMPRINT",FACE,{"disambiguationData":[TD([[makeQuery(id+"F0.imprint","IMPRINT",EDGE,{"derivedFrom":subQ0}),1.0]])]});}
            var Q76;
            {var subQ5=sQuery(id+"F0.wireOp",EDGE,"E27.left");Q76=makeQuery(id+"F0.imprint","IMPRINT",FACE,{"disambiguationData":[TD([[makeQuery(id+"F0.imprint","IMPRINT",EDGE,{"derivedFrom":subQ5}),1.0]])]});}
            var Q77;
            {var subQ0=sQuery(id+"F0.wireOp",EDGE,"E26.bottom");Q77=makeQuery(id+"F0.imprint","IMPRINT",FACE,{"disambiguationData":[TD([[makeQuery(id+"F0.imprint","IMPRINT",EDGE,{"derivedFrom":subQ0}),-1.0]])]});}
            var Q78;
            {var subQ0=sQuery(id+"F0.wireOp",EDGE,"E60");Q78=makeQuery(id+"F0.imprint","IMPRINT",FACE,{"disambiguationData":[TD([[makeQuery(id+"F0.imprint","IMPRINT",EDGE,{"derivedFrom":subQ0}),-1.0]])]});}
            var Q79;
            {var subQ0=sQuery(id+"F0.wireOp",EDGE,"E27.top");var subQ1=sQuery(id+"F0.wireOp",EDGE,"E26.left");var subQ2=makeQuery(id+"F0.imprint","INTERSECT",VERTEX,{"derivedFrom":[subQ1,subQ0]});Q79=makeQuery(id+"F0.imprint","IMPRINT",FACE,{"disambiguationData":[TD([[makeQuery(id+"F0.imprint","IMPRINT",EDGE,{"disambiguationData":[TD([[subQ2,-1.0]])],"derivedFrom":subQ1}),1.0]])]});}
            var Q80;
            {var subQ0=sQuery(id+"F0.wireOp",EDGE,"E61");Q80=makeQuery(id+"F0.imprint","IMPRINT",FACE,{"disambiguationData":[TD([[makeQuery(id+"F0.imprint","IMPRINT",EDGE,{"derivedFrom":subQ0}),-1.0]])]});}
            var Q81;
            {var subQ0=sQuery(id+"F0.wireOp",EDGE,"E62");Q81=makeQuery(id+"F0.imprint","IMPRINT",FACE,{"disambiguationData":[TD([[makeQuery(id+"F0.imprint","IMPRINT",EDGE,{"derivedFrom":subQ0}),-1.0]])]});}
            extrude(context, id + "F2", {"entities" : qUnion([Q0, Q1, Q2, Q3, Q4, Q5, Q6, Q7, Q8, Q9, Q10, Q11, Q12, Q13, Q14, Q15, Q16, Q17, Q18, Q19, Q20, Q21, Q22, Q23, Q24, Q25, Q26, Q27, Q28, Q29, Q30, Q31, Q32, Q33, Q34, Q35, Q36, Q37, Q38, Q39, Q40, Q41, Q42, Q43, Q44, Q45, Q46, Q47, Q48, Q49, Q50, Q51, Q52, Q53, Q54, Q55, Q56, Q57, Q58, Q59, Q60, Q61, Q62, Q63, Q64, Q65, Q66, Q67, Q68, Q69, Q70, Q71, Q72, Q73, Q74, Q75, Q76, Q77, Q78, Q79, Q80, Q81]), "depth" : 1 * mm});
        }
        {
            var Q0;
            Q0=makeQuery(id+"F1.opExtrude","SWEPT_EDGE",EDGE,{"disambiguationData":[OSD([sQuery(id+"F0.wireOp",EDGE,"E0.top"),sQuery(id+"F0.wireOp",EDGE,"E0.right")])]});
            var Q1;
            Q1=makeQuery(id+"F1.opExtrude","SWEPT_EDGE",EDGE,{"disambiguationData":[OSD([sQuery(id+"F0.wireOp",EDGE,"E0.bottom"),sQuery(id+"F0.wireOp",EDGE,"E0.left")])]});
            var Q2;
            Q2=makeQuery(id+"F1.opExtrude","SWEPT_EDGE",EDGE,{"disambiguationData":[OSD([sQuery(id+"F0.wireOp",EDGE,"E0.top"),sQuery(id+"F0.wireOp",EDGE,"E0.left")])]});
            var Q3;
            Q3=makeQuery(id+"F2.opExtrude","SWEPT_EDGE",EDGE,{"disambiguationData":[OSD([sQuery(id+"F0.wireOp",EDGE,"E0.top"),sQuery(id+"F0.wireOp",EDGE,"E0.left")])]});
            var Q4;
            Q4=makeQuery(id+"F2.opExtrude","SWEPT_EDGE",EDGE,{"disambiguationData":[OSD([sQuery(id+"F0.wireOp",EDGE,"E0.bottom"),sQuery(id+"F0.wireOp",EDGE,"E0.left")])]});
            var Q5;
            Q5=makeQuery(id+"F1.opExtrude","SWEPT_EDGE",EDGE,{"disambiguationData":[OSD([sQuery(id+"F0.wireOp",EDGE,"E0.bottom"),sQuery(id+"F0.wireOp",EDGE,"E0.right")])]});
            var Q6;
            Q6=makeQuery(id+"F2.opExtrude","SWEPT_EDGE",EDGE,{"disambiguationData":[OSD([sQuery(id+"F0.wireOp",EDGE,"E0.bottom"),sQuery(id+"F0.wireOp",EDGE,"E0.right")])]});
            var Q7;
            Q7=makeQuery(id+"F2.opExtrude","SWEPT_EDGE",EDGE,{"disambiguationData":[OSD([sQuery(id+"F0.wireOp",EDGE,"E0.top"),sQuery(id+"F0.wireOp",EDGE,"E0.right")])]});
            fillet(context, id + "F3", {"entities" : qUnion([Q0, Q1, Q2, Q3, Q4, Q5, Q6, Q7]), "radius" : 5 * mm, "tangentPropagation" : true, "allowEdgeOverflow" : false});
        }
        {
            var Q0;
            Q0=makeQuery(id+"F1.opExtrude","CAP_EDGE",EDGE,{"disambiguationData":[OSD([sQuery(id+"F0.wireOp",EDGE,"E0.bottom")])],"isStart":false});
            var Q1;
            Q1=makeQuery(id+"F1.opExtrude","CAP_EDGE",EDGE,{"disambiguationData":[OSD([sQuery(id+"F0.wireOp",EDGE,"E0.top")])],"isStart":false});
            chamfer(context, id + "F4", {"entities" : qUnion([Q0, Q1]), "width" : 2.5 * mm, "tangentPropagation" : true});
        }
    });
